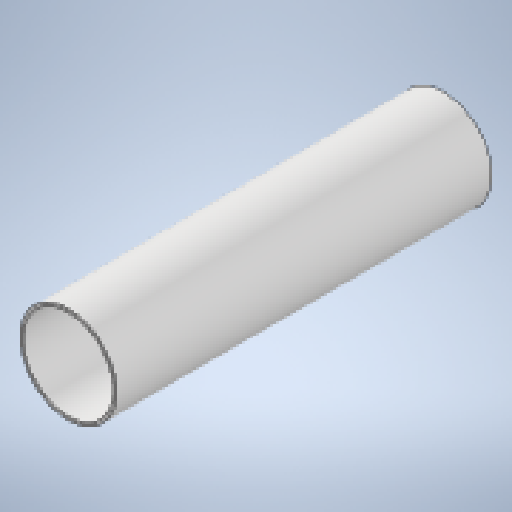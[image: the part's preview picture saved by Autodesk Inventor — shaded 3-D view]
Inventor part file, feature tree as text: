
AUTODESK INVENTOR PART (.ipt)
format: ipt  version: 2025.1 (Build 291241020, 241B)  size: 141,824 bytes
history: native  units: mm
features: extrude x1, sketch x1
ambient origin geometry x8: Origin, YZ Plane, XZ Plane, XY Plane, X Axis, Y Axis, Z Axis, Center Point
bodies: Solid1 (feature_tree)
feature tree (2):
  extrude  "Extrusion1"  Depth=415.0mm
  sketch  "Sketch1"  dims[d0=90.0mm d1=3.0mm d2=415.0mm d3=0.0mm]
